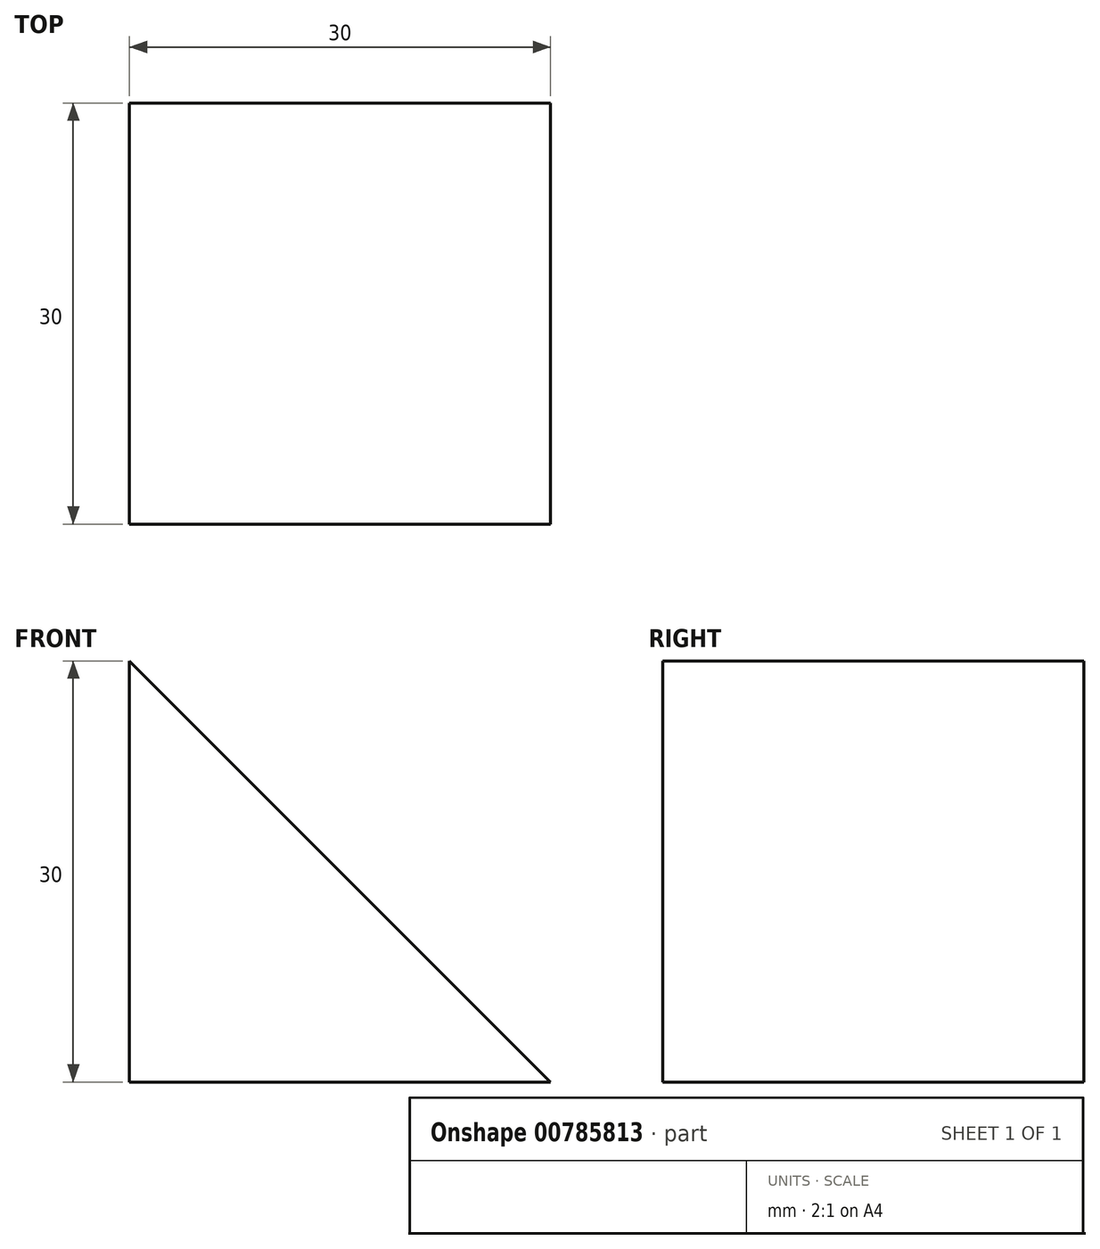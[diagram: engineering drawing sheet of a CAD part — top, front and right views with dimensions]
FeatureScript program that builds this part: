
annotation { "Feature Type Name" : "Feature", "Feature Type Description" : "" }
export const myFeature = defineFeature(function(context is Context, id is Id, definition is map)
    precondition{}
    {
        {
            var Q0;
            Q0=qCreatedBy(makeId("Front.planeOp"),FACE);
            var sketch = newSketch(context, id + "F0", { "sketchPlane" : qUnion([Q0])});
            skLineSegment(sketch, "E0", {"start": v(-15, -15) * mm, "end": v(15, -15) * mm});
            skLineSegment(sketch, "E1", {"start": v(-15, -15) * mm, "end": v(-15, 15) * mm});
            skLineSegment(sketch, "E2", {"start": v(-15, 15) * mm, "end": v(15, -15) * mm});
            skSolve(sketch);
        }
        {
            var Q0;
            Q0=makeQuery(id+"F0.imprint","IMPRINT",FACE,{"disambiguationData":[TD([[makeQuery(id+"F0.imprint","IMPRINT",EDGE,{"derivedFrom":sQuery(id+"F0.wireOp",EDGE,"E0")}),1.0]])]});
            extrude(context, id + "F1", {"entities" : qUnion([Q0]), "depth" : 30 * mm, "offsetDistance" : 25 * mm});
        }
    });
